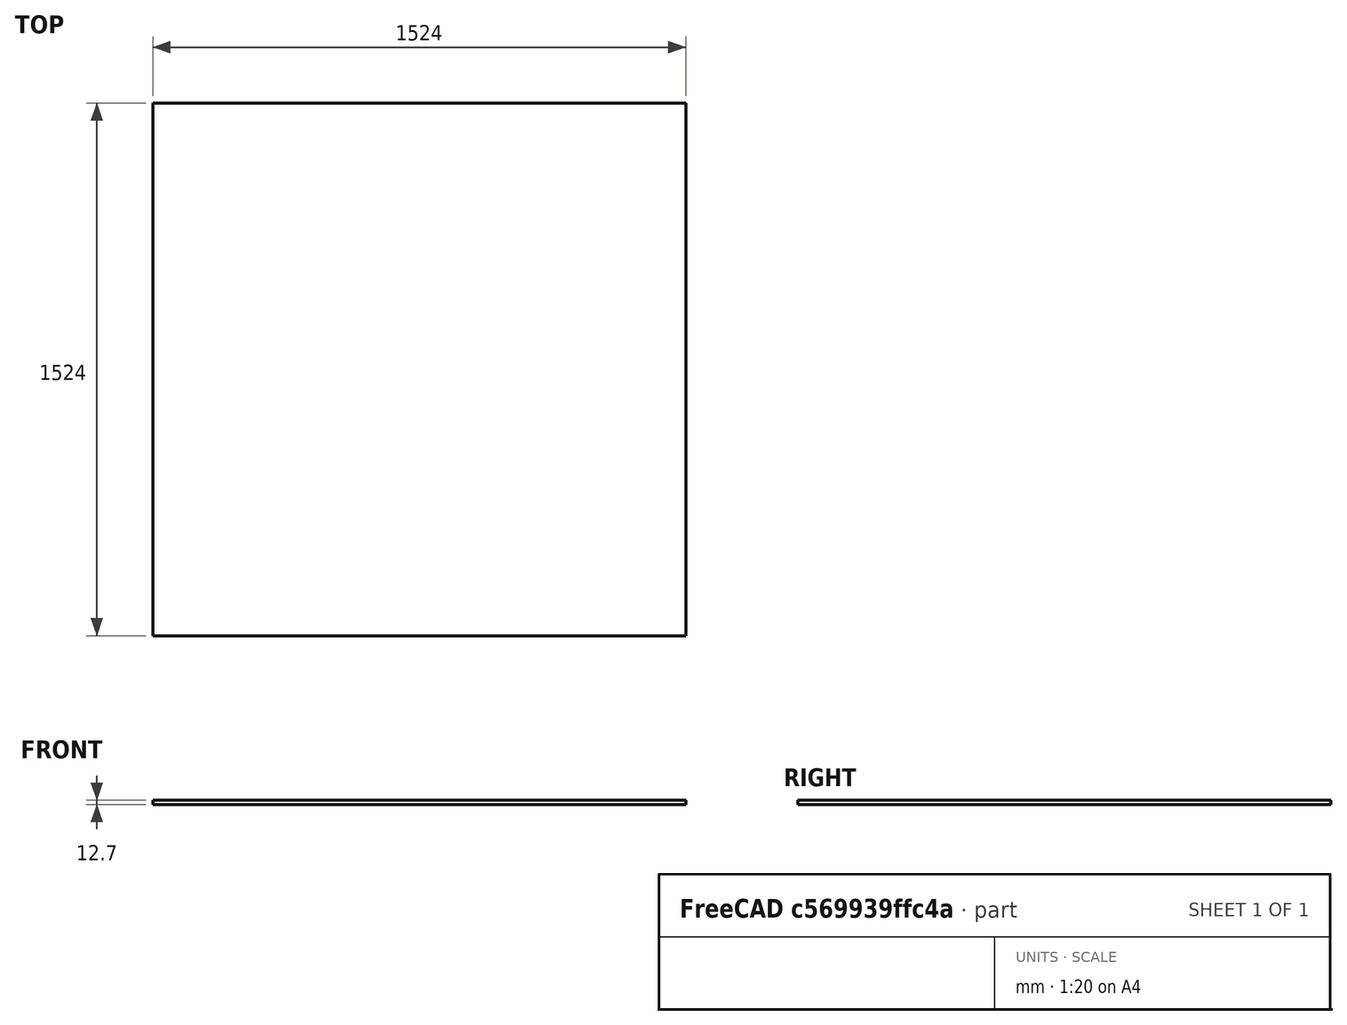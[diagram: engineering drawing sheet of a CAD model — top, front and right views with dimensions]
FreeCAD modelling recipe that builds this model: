
FCSTD DOCUMENT  (FreeCAD 0.19R24291 (Git))
Label: plywoodSheet5x5x0.5
License: All rights reserved
LicenseURL: http://en.wikipedia.org/wiki/All_rights_reserved
objects: Sketcher::SketchObject×1, PartDesign::Pad×1, PartDesign::Body×1
note: 4 computed .brp shape members not serialized (recipe doc carries the construction recipe); baked Part::Feature solids carry a one-line shape summary decoded from their .brp

FEATURE [Sketcher::SketchObject] Sketch
  FullyConstrained = true
  MapMode = 5
  Support = -> [XY_Plane]
  expr: Constraints[9] = 5 * 12 * 25.4
  sketch-geometry (4):
    g0: LineSegment StartX=0 StartY=0 StartZ=0 EndX=1524 EndY=0 EndZ=0
    g1: LineSegment StartX=1524 StartY=0 StartZ=0 EndX=1524 EndY=1524 EndZ=0
    g2: LineSegment StartX=1524 StartY=1524 StartZ=0 EndX=0 EndY=1524 EndZ=0
    g3: LineSegment StartX=0 StartY=1524 StartZ=0 EndX=0 EndY=0 EndZ=0
  constraints (11):
    c: Coincident(g0,g1)
    c: Coincident(g1,g2)
    c: Coincident(g2,g3)
    c: Coincident(g3,g0)
    c: Horizontal(g0)
    c: Horizontal(g2)
    c: Vertical(g1)
    c: Vertical(g3)
    c: Coincident(g0,g-1)
    c: DistanceX(g0,g0) = 1524
    c: Equal(g3,g0)
FEATURE [PartDesign::Pad] Pad
  Direction = (1,1,1)
  Length = 12.7
  Length2 = 100
  Profile = -> Sketch
  Type = 0
  expr: Length = 1 / 2 * 25.4
FEATURE [PartDesign::Body] Body
  Group = -> [Sketch,Pad]
  Origin = -> Origin
  Tip = -> Pad
